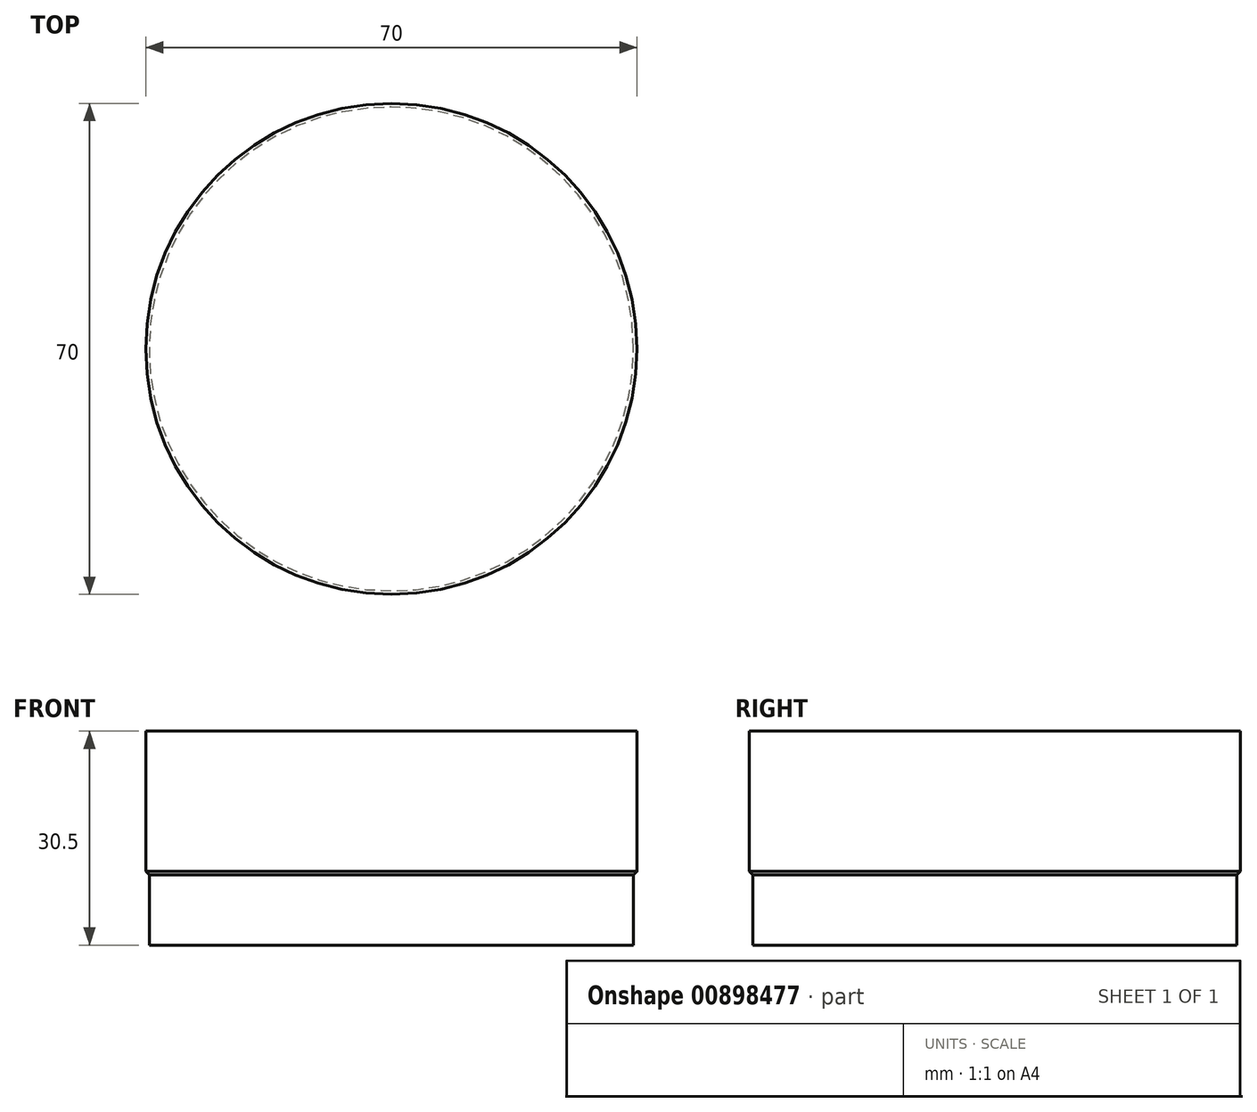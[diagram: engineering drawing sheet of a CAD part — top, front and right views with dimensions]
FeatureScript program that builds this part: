
annotation { "Feature Type Name" : "Feature", "Feature Type Description" : "" }
export const myFeature = defineFeature(function(context is Context, id is Id, definition is map)
    precondition{}
    {
        {
            var Q0;
            Q0=qCreatedBy(makeId("Front.planeOp"),FACE);
            var sketch = newSketch(context, id + "F0", { "sketchPlane" : qUnion([Q0])});
            skLineSegment(sketch, "E0", {"start": v(0, 0) * mm, "end": v(0, 30.5) * mm, "construction": true});
            skLineSegment(sketch, "E1", {"start": v(128.6, 222.53) * mm, "end": v(130.4, 225.61) * mm});
            skLineSegment(sketch, "E2", {"start": v(0, 0) * mm, "end": v(34.5, 0) * mm});
            skLineSegment(sketch, "E3", {"start": v(34.5, 0) * mm, "end": v(34.5, 10) * mm});
            skLineSegment(sketch, "E4", {"start": v(34.5, 10) * mm, "end": v(35, 10.5) * mm});
            skLineSegment(sketch, "E5", {"start": v(35, 30.5) * mm, "end": v(35, 10.5) * mm});
            skLineSegment(sketch, "E6", {"start": v(0, 30.5) * mm, "end": v(35, 30.5) * mm});
            skLineSegment(sketch, "E7", {"start": v(0, 30.5) * mm, "end": v(0, 0) * mm});
            skSolve(sketch);
        }
        {
            var Q0;
            Q0=makeQuery(id+"F0.imprint","IMPRINT",FACE,{"disambiguationData":[TD([[makeQuery(id+"F0.imprint","IMPRINT",EDGE,{"derivedFrom":sQuery(id+"F0.wireOp",EDGE,"E2")}),1.0]])]});
            var Q1;
            Q1=sQuery(id+"F0.wireOp",EDGE,"E7");
            revolve(context, id + "F1", {"surfaceOperationType" : NewSurfaceOperationType.NEW, "entities" : qUnion([Q0]), "axis" : qUnion([Q1]), "revolveType" : RevolveType.FULL});
        }
    });
